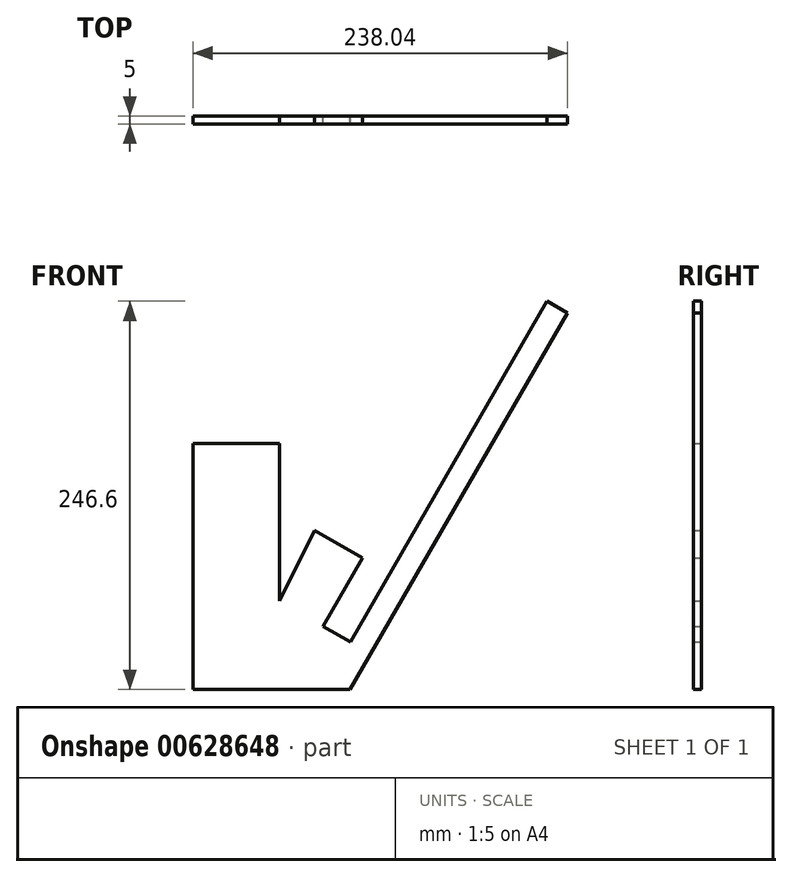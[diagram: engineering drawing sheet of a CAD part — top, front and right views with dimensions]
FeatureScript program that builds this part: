
annotation { "Feature Type Name" : "Feature", "Feature Type Description" : "" }
export const myFeature = defineFeature(function(context is Context, id is Id, definition is map)
    precondition{}
    {
        {
            var Q0;
            Q0=qCreatedBy(makeId("Front.planeOp"),FACE);
            var sketch = newSketch(context, id + "F0", { "sketchPlane" : qUnion([Q0])});
            skLineSegment(sketch, "E0", {"start": v(0, 0) * mm, "end": v(100, 0) * mm});
            skLineSegment(sketch, "E1", {"start": v(100, 0) * mm, "end": v(238.04, 239.1) * mm});
            skLineSegment(sketch, "E2", {"start": v(238.04, 239.1) * mm, "end": v(225.05, 246.6) * mm});
            skLineSegment(sketch, "E3", {"start": v(55, 56.1) * mm, "end": v(55, 156.1) * mm});
            skLineSegment(sketch, "E4", {"start": v(55, 156.1) * mm, "end": v(0, 156.1) * mm});
            skLineSegment(sketch, "E5", {"start": v(0, 156.1) * mm, "end": v(0, 0) * mm});
            skLineSegment(sketch, "E6", {"start": v(225.05, 246.6) * mm, "end": v(100.05, 30.1) * mm});
            skLineSegment(sketch, "E7", {"start": v(100.05, 30.1) * mm, "end": v(82.73, 40.1) * mm});
            skLineSegment(sketch, "E8", {"start": v(82.73, 40.1) * mm, "end": v(107.73, 83.4) * mm});
            skLineSegment(sketch, "E9", {"start": v(107.73, 83.4) * mm, "end": v(77.42, 100.9) * mm});
            skLineSegment(sketch, "E10", {"start": v(77.42, 100.9) * mm, "end": v(55, 56.1) * mm});
            skLineSegment(sketch, "E11", {"start": v(238.04, 239.1) * mm, "end": v(118.32, 308.22) * mm, "construction": true});
            skSolve(sketch);
        }
        {
            var Q0;
            Q0=qSketchRegion(id+"F0",true);
            extrude(context, id + "F1", {"entities" : qUnion([Q0]), "depth" : 5 * mm, "offsetDistance" : 25 * mm});
        }
    });
